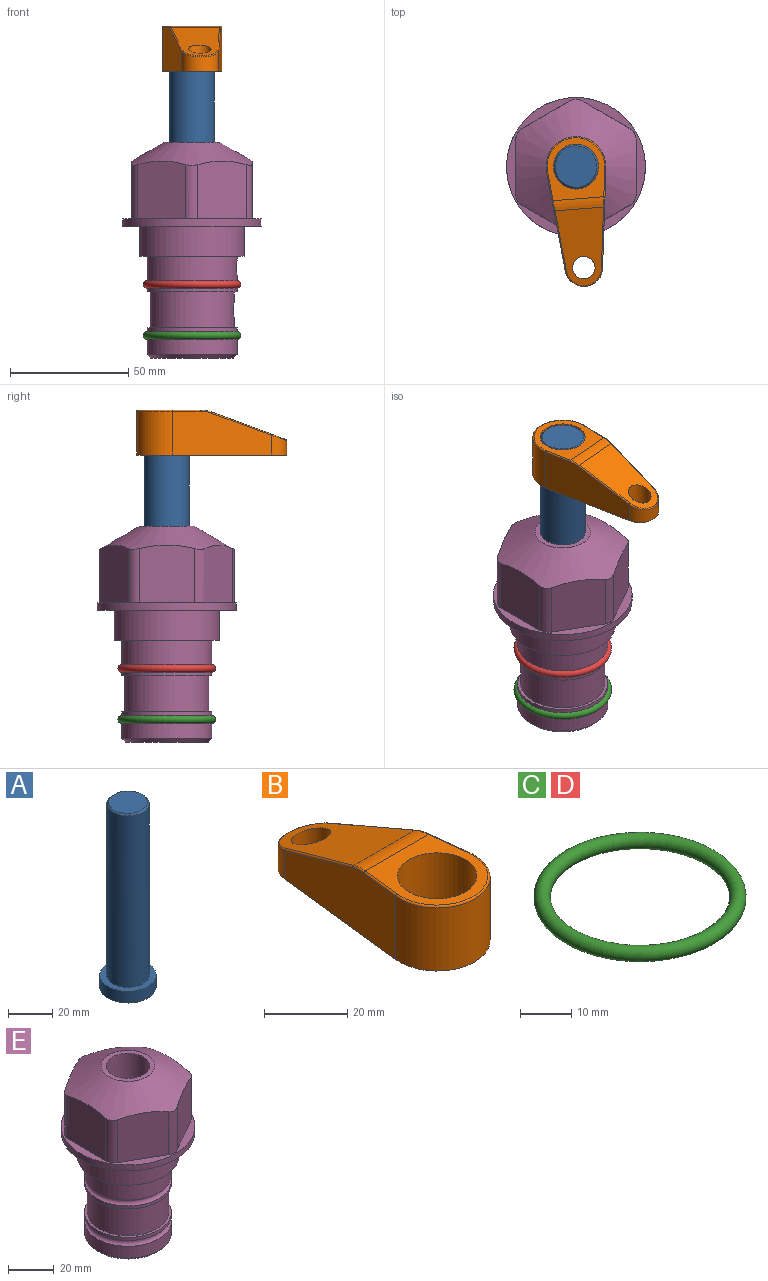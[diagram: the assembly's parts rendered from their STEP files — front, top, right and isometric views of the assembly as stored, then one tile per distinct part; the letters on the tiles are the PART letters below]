
ASSEMBLY  parts=5 mates=3
PART A: 6 faces, bbox 25.4x25.4x101.6 mm
  f0: plane 17.46x17.46mm, normal (0,0,1), area 239.5mm2, adj f5
  f1: plane 25.4x25.4mm, normal (0,0,-1), area 506.7mm2, adj f2
  f2: cylinder r=12.7mm len=25.4mm, axis (0,0,1), area 506.7mm2, adj f1,f3
  f3: plane 25.4x25.4mm, normal (0,0,1), area 221.7mm2, adj f2,f4
  f4: cylinder r=9.53mm len=94.46mm, axis (0,0,1), area 5653mm2, adj f3,f5
  f5: cone r=8.73mm half-angle=45deg, axis (0,0,-1), area 64.4mm2, adj f0,f4
PART B: 44 faces, bbox 27.5x64.5x19.1 mm
  f0: plane 2.3x0.95mm, normal (0,0,-1), area 1mm2, adj f25,f30,f34
  f1: plane 63.5x25.4mm, normal (0,0,-1), area 561.7mm2, adj f2,f3,f4,f5,f6,f7,f19,f20
  f2: cylinder r=12.7mm len=25.4mm, axis (0,0,-1), area 792.2mm2, adj f1,f3,f5,f13
  f3: plane 42.33x18.54mm, normal (0.99,0.11,0), area 647mm2, adj f1,f2,f4,f11,f12,f14
  f4: cylinder r=7.94mm len=15.78mm, axis (0,0,-1), area 158.6mm2, adj f1,f3,f5,f16
  f5: plane 42.33x18.54mm, normal (-0.99,0.11,0), area 647mm2, adj f1,f2,f4,f15,f17,f18
  f6: cylinder r=9.53mm len=19.05mm, axis (0,0,-1), area 1140.1mm2, adj f1,f8
  f7: cylinder r=4.76mm len=10.98mm, axis (0,0,-1), area 276.1mm2, adj f1,f9
  f8: plane 25.83x24.38mm, normal (0,0,1), area 262.2mm2, adj f6,f10,f11,f13,f15
  f9: plane 32.49x20.55mm, normal (0,0.34,0.94), area 489.9mm2, adj f7,f10,f14,f16,f18
  f10: cylinder r=12.7mm len=21.49mm, axis (-1,0,0), area 93.2mm2, adj f8,f9,f12,f17
  f11: cylinder r=0.51mm len=12.34mm, axis (0.11,-0.99,0), area 9.9mm2, adj f3,f8,f12,f13
  f12: bspline ~7.62x1.64mm, area 3.5mm2, adj f3,f10,f11,f14
  f13: torus R=12.19mm, axis (0,0,1), area 33.6mm2, adj f2,f8,f11,f15
  f14: cylinder r=0.51mm len=26.01mm, axis (0.1,-0.93,0.34), area 21.6mm2, adj f3,f9,f12,f16
  f15: cylinder r=0.51mm len=12.34mm, axis (0.11,0.99,0), area 9.9mm2, adj f5,f8,f13,f17
  f16: bspline ~15.78x7.05mm, area 15.7mm2, adj f4,f9,f14,f18
  f17: bspline ~7.62x1.64mm, area 3.5mm2, adj f5,f10,f15,f18
  f18: cylinder r=0.51mm len=26.01mm, axis (0.1,0.93,-0.34), area 21.6mm2, adj f5,f9,f16,f17
  f19: plane 21.6x14.29mm, normal (-0.99,-0.11,0), area 242.6mm2, adj f1,f26,f28,f34,f36,f38
  f20: plane 21.6x14.29mm, normal (0.99,-0.11,0), area 242.6mm2, adj f1,f27,f29,f37,f39,f41
  f21: cylinder r=12.7mm len=14.29mm, axis (0,0,-1), area 173.2mm2, adj f1,f26,f27,f30,f31,f33
  f22: cylinder r=7.94mm len=7.63mm, axis (0,0,-1), area 53.8mm2, adj f1,f28,f29,f42
  f23: plane 2.3x0.95mm, normal (0,0,-1), area 1mm2, adj f25,f33,f37
  f24: plane 17.94x12.32mm, normal (0,-0.34,-0.94), area 191.2mm2, adj f25,f38,f41,f42
  f25: cylinder r=9.53mm len=12.93mm, axis (-1,0,0), area 37.5mm2, adj f0,f23,f24,f31,f36,f39
  f26: cylinder r=1.59mm len=14.29mm, axis (0,0,-1), area 49mm2, adj f1,f19,f21,f32
  f27: cylinder r=1.59mm len=14.29mm, axis (0,0,-1), area 49mm2, adj f1,f20,f21,f35
  f28: cylinder r=1.59mm len=7.28mm, axis (0,0,-1), area 22.1mm2, adj f1,f19,f22,f40
  f29: cylinder r=1.59mm len=7.28mm, axis (0,0,-1), area 22.1mm2, adj f1,f20,f22,f43
  f30: torus R=14.29mm, axis (0,0,1), area 5.8mm2, adj f0,f21,f31,f32
  f31: bspline ~11.06x2.73mm, area 20.8mm2, adj f21,f25,f30,f33
  f32: sphere r=1.59mm, area 5.4mm2, adj f26,f30,f34
  f33: torus R=14.29mm, axis (0,0,1), area 5.8mm2, adj f21,f23,f31,f35
  f34: cylinder r=1.59mm len=1.68mm, axis (-0.11,0.99,0), area 2.4mm2, adj f0,f19,f32,f36
  f35: sphere r=1.59mm, area 5.4mm2, adj f27,f33,f37
  f36: bspline ~5.82x2.33mm, area 7.7mm2, adj f19,f25,f34,f38
  f37: cylinder r=1.59mm len=1.68mm, axis (0.11,0.99,0), area 2.4mm2, adj f20,f23,f35,f39
  f38: cylinder r=1.59mm len=18.33mm, axis (0.1,-0.93,0.34), area 46.7mm2, adj f19,f24,f36,f40
  f39: bspline ~5.82x2.33mm, area 7.7mm2, adj f20,f25,f37,f41
  f40: sphere r=1.59mm, area 3.6mm2, adj f28,f38,f42
  f41: cylinder r=1.59mm len=18.33mm, axis (0.1,0.93,-0.34), area 46.7mm2, adj f20,f24,f39,f43
  f42: bspline ~8.31x1.84mm, area 15.3mm2, adj f22,f24,f40,f43
  f43: sphere r=1.59mm, area 3.6mm2, adj f29,f41,f42
PART C: 1 faces, bbox 44.7x44.7x3.2 mm
  f0: torus R=19.05mm, axis (0,0,1), area 1193.9mm2
PART D: same geometry as C
PART E: 36 faces, bbox 58.7x58.7x91.2 mm
  f0: cylinder r=17.78mm len=35.56mm, axis (0,0,1), area 1670.8mm2, adj f23,f24,f31
  f1: cylinder r=19.05mm len=38.1mm, axis (0,0,1), area 1191.9mm2, adj f26,f27,f30
  f2: plane 58.66x58.66mm, normal (0,0,-1), area 1150.6mm2, adj f3,f28
  f3: cylinder r=29.33mm len=58.66mm, axis (0,0,-1), area 585.1mm2, adj f2,f4
  f4: plane 58.66x58.66mm, normal (0,0,1), area 475.9mm2, adj f3,f5,f6,f7,f8,f9,f10,f11
  f5: plane 24.5x20.32mm, normal (-0.5,0.87,0), area 562.8mm2, adj f4,f15,f16,f17
  f6: plane 24.5x20.32mm, normal (0.5,0.87,0), area 562.8mm2, adj f4,f14,f15,f17
  f7: plane 24.5x23.48mm, normal (1,0,0), area 562.8mm2, adj f4,f13,f14,f17
  f8: plane 24.5x20.32mm, normal (0.5,-0.87,0), area 562.8mm2, adj f4,f12,f13,f17
  f9: plane 24.5x20.32mm, normal (-0.5,-0.87,0), area 562.8mm2, adj f4,f11,f12,f17
  f10: plane 24.5x23.48mm, normal (-1,0,0), area 562.8mm2, adj f4,f11,f16,f17
  f11: cylinder r=5.08mm len=23.01mm, axis (0,0,-1), area 121.2mm2, adj f4,f9,f10,f17
  f12: cylinder r=5.08mm len=23.01mm, axis (0,0,-1), area 121.2mm2, adj f4,f8,f9,f17
  f13: cylinder r=5.08mm len=23.01mm, axis (0,0,-1), area 121.2mm2, adj f4,f7,f8,f17
  f14: cylinder r=5.08mm len=23.01mm, axis (0,0,-1), area 121.2mm2, adj f4,f6,f7,f17
  f15: cylinder r=5.08mm len=23.01mm, axis (0,0,-1), area 121.2mm2, adj f4,f5,f6,f17
  f16: cylinder r=5.08mm len=23.01mm, axis (0,0,-1), area 121.2mm2, adj f4,f5,f10,f17
  f17: cone r=11.73mm half-angle=60deg, axis (0,0,-1), area 2071.8mm2, adj f5,f6,f7,f8,f9,f10,f11,f12
  f18: plane 23.46x23.46mm, normal (0,0,1), area 147.4mm2, adj f17,f35
  f19: plane 34.93x34.93mm, normal (0,0,-1), area 958mm2, adj f29
  f20: cylinder r=19.05mm len=38.1mm, axis (0,0,1), area 760.1mm2, adj f21,f29
  f21: torus R=19.05mm, axis (0,0,1), area 565.3mm2, adj f20,f22
  f22: cylinder r=19.05mm len=38.1mm, axis (0,0,1), area 190mm2, adj f21,f23
  f23: plane 38.1x38.1mm, normal (0,0,1), area 146.9mm2, adj f0,f22
  f24: plane 38.1x38.1mm, normal (0,0,-1), area 146.9mm2, adj f0,f25
  f25: cylinder r=19.05mm len=38.1mm, axis (0,0,1), area 190mm2, adj f24,f26
  f26: torus R=19.05mm, axis (0,0,1), area 565.3mm2, adj f1,f25
  f27: plane 44.45x44.45mm, normal (0,0,-1), area 411.7mm2, adj f1,f28
  f28: cylinder r=22.23mm len=44.45mm, axis (0,0,1), area 1773.5mm2, adj f2,f27
  f29: cone r=19.05mm half-angle=45deg, axis (0,0,1), area 257.5mm2, adj f19,f20
  f30: cylinder r=3.17mm len=6.75mm, axis (-1,0,0), area 128mm2, adj f1,f33
  f31: cylinder r=3.17mm len=6.35mm, axis (-1,0,0), area 102.5mm2, adj f0,f33
  f32: plane 25.4x25.4mm, normal (0,0,1), area 506.7mm2, adj f33
  f33: cylinder r=12.7mm len=66.42mm, axis (0,0,-1), area 5236.2mm2, adj f30,f31,f32,f34
  f34: cone r=9.53mm half-angle=30deg, axis (0,0,-1), area 443.4mm2, adj f33,f35
  f35: cylinder r=9.53mm len=19.05mm, axis (0,0,-1), area 849mm2, adj f18,f34
PLACE A rot(axis=(0,0,-1),85.6deg) t=(0,0,11.11)mm
PLACE B rot(axis=(0,0,-1),175.6deg) t=(0,0,65.72)mm
PLACE C t=(0,0,-21.59)mm
PLACE D at identity
PLACE E at identity fixed
MATE fastened C.f0 <-> E.f0  axis (0,0,1) through (0,0,-46.1)mm
MATE cylindrical A.f2 <-> E.f0  axis (0,0,1) through (0,0,36.74)mm
MATE fastened B.f2 <-> A.f2  axis (0,0,1) through (0,0,84.77)mm
